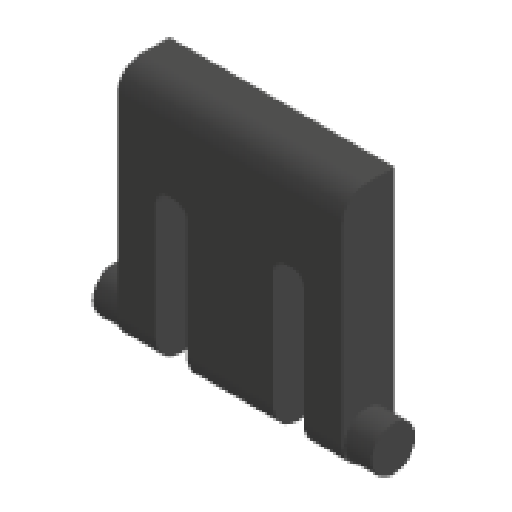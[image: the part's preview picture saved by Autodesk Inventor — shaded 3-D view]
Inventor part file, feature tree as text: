
AUTODESK INVENTOR PART (.ipt)
format: ipt  version: 2025 (Build 290162000, 162)  size: 193,536 bytes
history: native  units: mm
features: extrude x4, sketch x4, fillet x2, mirror x1
ambient origin geometry x8: Origin, YZ Plane, XZ Plane, XY Plane, X Axis, Y Axis, Z Axis, Center Point
bodies: Solid1 (feature_tree)
feature tree (11):
  extrude  "Extrusion1"  Depth=11.7mm
  extrude  "Extrusion3"  Depth=2.7mm
  extrude  "Extrusion4"  Depth=1.4mm TaperAngle=0.0deg
  mirror  "Mirror1"
  extrude  "Extrusion5"  Depth=1.6mm
  fillet  "Fillet1"  Radius=8.0mm
  fillet  "Fillet3"  [1 undecoded]
  sketch  "Sketch1"  dims[d0=12.5mm d1=11.7mm]
  sketch  "Sketch3"  dims[d2=2.7mm d3=0.0mm d10=2.3mm]
  sketch  "Sketch4"  dims[d11=0.1mm d13=1.4mm d14=0.0mm]
  sketch  "Sketch6"  dims[d18=2.0mm d19=1.6mm d20=8.0mm d21=0.0mm d22=0.0mm d23=0.1mm d32=3.0mm d34=3.0mm d35=0.0mm d36=0.0mm d37=0.6mm d40=1.2mm d49=0.2mm d50=2.0mm d51=5.0mm]
note: 1 required parameter value undecoded (feature->parameter linkage not recoverable at this tier; creation-order binding heuristic only, values carry confidence <= 0.55)
